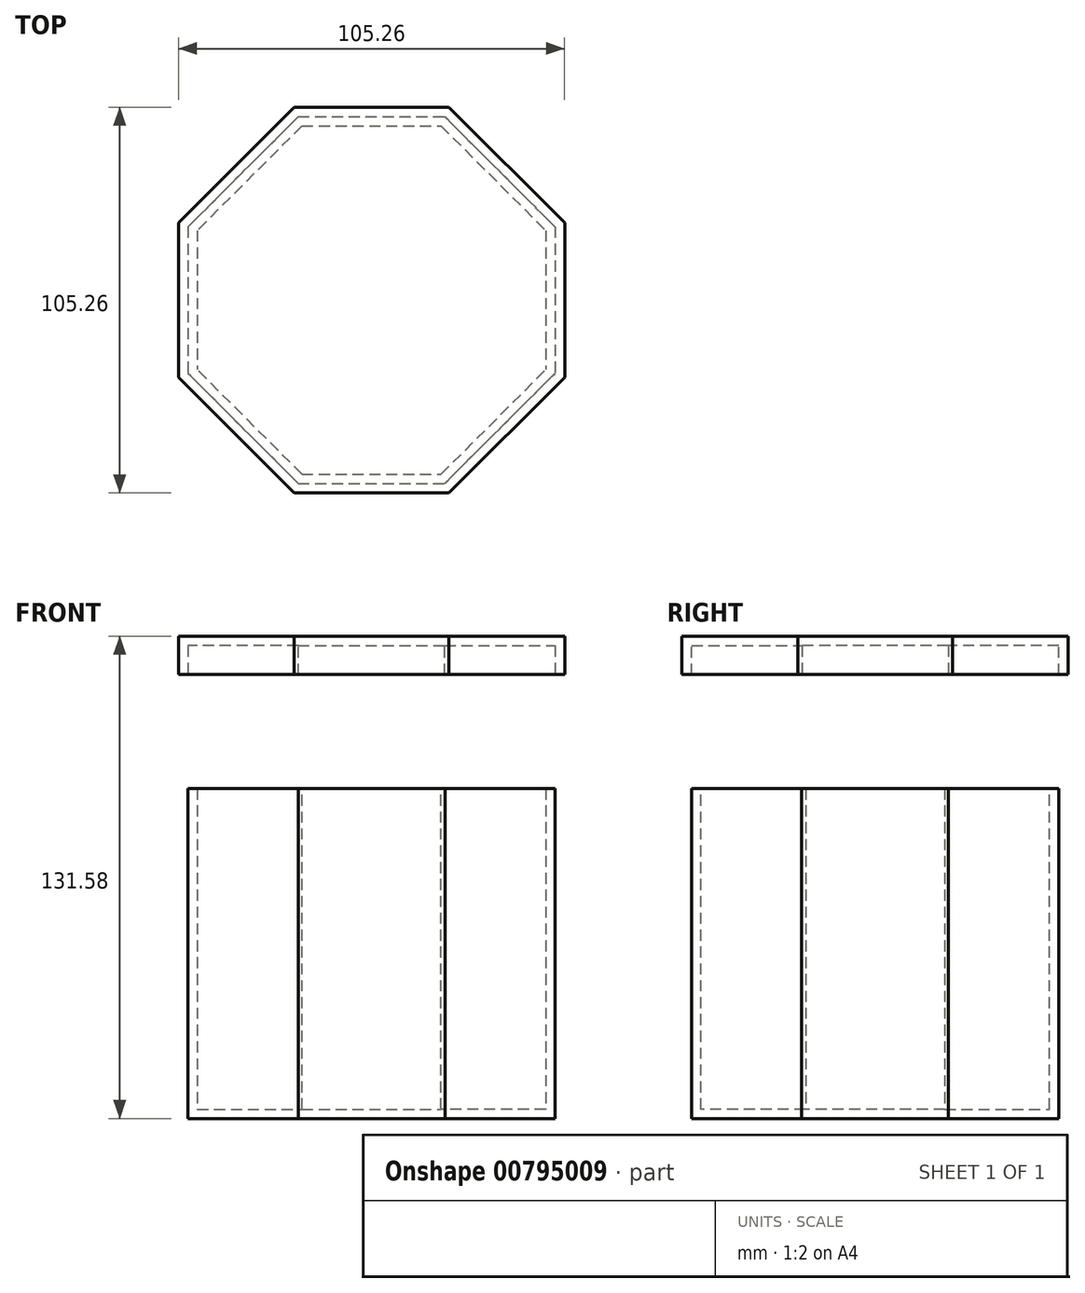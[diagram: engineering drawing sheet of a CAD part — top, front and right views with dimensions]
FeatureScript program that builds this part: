
annotation { "Feature Type Name" : "Feature", "Feature Type Description" : "" }
export const myFeature = defineFeature(function(context is Context, id is Id, definition is map)
    precondition{}
    {
        {
            var Q0;
            Q0=qCreatedBy(makeId("Top.planeOp"),FACE);
            var sketch = newSketch(context, id + "F0", { "sketchPlane" : qUnion([Q0])});
            skLineSegment(sketch, "E0.bottom", {"start": v(-50, 50) * mm, "end": v(50, 50) * mm});
            skLineSegment(sketch, "E0.top", {"start": v(-50, -50) * mm, "end": v(50, -50) * mm});
            skLineSegment(sketch, "E0.left", {"start": v(-50, 50) * mm, "end": v(-50, -50) * mm});
            skLineSegment(sketch, "E0.right", {"start": v(50, 50) * mm, "end": v(50, -50) * mm});
            skSolve(sketch);
        }
        {
            var Q0;
            Q0=makeQuery(id+"F0.imprint","IMPRINT",FACE,{"disambiguationData":[TD([[makeQuery(id+"F0.imprint","IMPRINT",EDGE,{"derivedFrom":sQuery(id+"F0.wireOp",EDGE,"E0.bottom")}),-1.0]])]});
            extrude(context, id + "F1", {"entities" : qUnion([Q0]), "depth" : 90 * mm, "offsetDistance" : 25 * mm});
        }
        {
            var Q0;
            Q0=makeQuery(id+"F1.opExtrude","SWEPT_EDGE",EDGE,{"disambiguationData":[OSD([sQuery(id+"F0.wireOp",EDGE,"E0.bottom"),sQuery(id+"F0.wireOp",EDGE,"E0.left")])]});
            var Q1;
            Q1=makeQuery(id+"F1.opExtrude","SWEPT_EDGE",EDGE,{"disambiguationData":[OSD([sQuery(id+"F0.wireOp",EDGE,"E0.bottom"),sQuery(id+"F0.wireOp",EDGE,"E0.right")])]});
            var Q2;
            Q2=makeQuery(id+"F1.opExtrude","SWEPT_EDGE",EDGE,{"disambiguationData":[OSD([sQuery(id+"F0.wireOp",EDGE,"E0.top"),sQuery(id+"F0.wireOp",EDGE,"E0.right")])]});
            var Q3;
            Q3=makeQuery(id+"F1.opExtrude","SWEPT_EDGE",EDGE,{"disambiguationData":[OSD([sQuery(id+"F0.wireOp",EDGE,"E0.top"),sQuery(id+"F0.wireOp",EDGE,"E0.left")])]});
            chamfer(context, id + "F2", {"entities" : qUnion([Q0, Q1, Q2, Q3]), "width" : 30 * mm, "tangentPropagation" : true});
        }
        {
            var Q0;
            Q0=makeQuery(id+"F1.opExtrude","CAP_FACE",FACE,{"disambiguationData":[OSD([sQuery(id+"F0.wireOp",EDGE,"E0.bottom"),sQuery(id+"F0.wireOp",EDGE,"E0.top"),sQuery(id+"F0.wireOp",EDGE,"E0.left"),sQuery(id+"F0.wireOp",EDGE,"E0.right")])],"isStart":false});
            shell(context, id + "F3", {"entities" : qUnion([Q0]), "thickness" : 2.5 * mm});
        }
        {
            var Q0;
            Q0=makeQuery(id+"F1.opExtrude","CAP_FACE",FACE,{"disambiguationData":[OSD([sQuery(id+"F0.wireOp",EDGE,"E0.bottom"),sQuery(id+"F0.wireOp",EDGE,"E0.top"),sQuery(id+"F0.wireOp",EDGE,"E0.left"),sQuery(id+"F0.wireOp",EDGE,"E0.right")])],"isStart":false});
            cPlane(context, id + "F4", {"entities" : qUnion([Q0]), "cplaneType" : CPlaneType.OFFSET, "offset" : 25 * mm, "width" : 150 * mm, "height" : 150 * mm});
        }
        {
            var Q0;
            Q0=qCreatedBy(id+"F4.planeOp",FACE);
            var sketch = newSketch(context, id + "F5", { "sketchPlane" : qUnion([Q0])});
            skLineSegment(sketch, "E1.bottom", {"start": v(-50, 50) * mm, "end": v(50, 50) * mm});
            skLineSegment(sketch, "E1.top", {"start": v(-50, -50) * mm, "end": v(50, -50) * mm});
            skLineSegment(sketch, "E1.left", {"start": v(-50, 50) * mm, "end": v(-50, -50) * mm});
            skLineSegment(sketch, "E1.right", {"start": v(50, 50) * mm, "end": v(50, -50) * mm});
            skSolve(sketch);
        }
        {
            var Q0;
            Q0=makeQuery(id+"F5.imprint","IMPRINT",FACE,{"disambiguationData":[TD([[makeQuery(id+"F5.imprint","IMPRINT",EDGE,{"derivedFrom":sQuery(id+"F5.wireOp",EDGE,"E1.bottom")}),-1.0]])]});
            extrude(context, id + "F6", {"entities" : qUnion([Q0]), "depth" : 10 * mm, "offsetDistance" : 25 * mm});
        }
        {
            var Q0;
            Q0=makeQuery(id+"F6.opExtrude","SWEPT_EDGE",EDGE,{"disambiguationData":[OSD([sQuery(id+"F5.wireOp",EDGE,"E1.top"),sQuery(id+"F5.wireOp",EDGE,"E1.left")])]});
            var Q1;
            Q1=makeQuery(id+"F6.opExtrude","SWEPT_EDGE",EDGE,{"disambiguationData":[OSD([sQuery(id+"F5.wireOp",EDGE,"E1.bottom"),sQuery(id+"F5.wireOp",EDGE,"E1.left")])]});
            var Q2;
            Q2=makeQuery(id+"F6.opExtrude","SWEPT_EDGE",EDGE,{"disambiguationData":[OSD([sQuery(id+"F5.wireOp",EDGE,"E1.bottom"),sQuery(id+"F5.wireOp",EDGE,"E1.right")])]});
            var Q3;
            Q3=makeQuery(id+"F6.opExtrude","SWEPT_EDGE",EDGE,{"disambiguationData":[OSD([sQuery(id+"F5.wireOp",EDGE,"E1.top"),sQuery(id+"F5.wireOp",EDGE,"E1.right")])]});
            chamfer(context, id + "F7", {"entities" : qUnion([Q0, Q1, Q2, Q3]), "width" : 30 * mm, "tangentPropagation" : true});
        }
        {
            var Q0;
            Q0=makeQuery(id+"F6.opExtrude","CAP_FACE",FACE,{"disambiguationData":[OSD([sQuery(id+"F5.wireOp",EDGE,"E1.bottom"),sQuery(id+"F5.wireOp",EDGE,"E1.top"),sQuery(id+"F5.wireOp",EDGE,"E1.left"),sQuery(id+"F5.wireOp",EDGE,"E1.right")])],"isStart":true});
            shell(context, id + "F8", {"entities" : qUnion([Q0]), "thickness" : 2.5 * mm});
        }
        {
            var Q0;
            Q0=makeQuery(id+"F6.opExtrude","SWEPT_BODY",BODY,{"disambiguationData":[OSD([sQuery(id+"F5.wireOp",EDGE,"E1.bottom"),sQuery(id+"F5.wireOp",EDGE,"E1.top"),sQuery(id+"F5.wireOp",EDGE,"E1.left"),sQuery(id+"F5.wireOp",EDGE,"E1.right")])]});
            var Q1;
            Q1=qCreatedBy(makeId("Origin.pointOp"),VERTEX);
            transform(context, id + "F9", {"entities" : qUnion([Q0]), "transformType" : TransformType.SCALE_UNIFORMLY, "scale" : 1.05, "scalePoint" : qUnion([Q1]), "makeCopy" : false});
        }
    });
